# Revit family: МФУ, копир настольный формата А3
name_source: partatom
category: Оборудование
revit_build: Autodesk Revit 2017 (Build: 20170419_0315(x64)
units: mm (PartAtom-declared; Revit-internal decimal feet)

## family parameters
Всегда вертикально = Да
На основе рабочей плоскости = Нет
Общий = Нет
При загрузке вырезать с полостями = Нет
Размер круглого соединителя = Использовать диаметр
Тип детали = Нормальный
Точка расчета площади = Нет

## types (1)
- -
    bialy = xero_szary
    blekitny = xero_blekitny
    czerwony = xero_czerwony
    lcd = xero_lcd
    niebieski ciemniejszy majtkowy = xero_ciemniejsze majty
    niebieski ciemny przycisk = xero_niebieski przycisk
    niebieski majtkowy = xero_niebieski majtkowy
    niebieskie szkolo = Glass, Green
    Высота = 558 мм
    Глубина = 587 мм
    Единицы = шт.
    Задание = ЭМ
    Изготовитель = Severin
    Мощность номинальная = 1000 Вт
    Наименование = Многофункциональное устройство формата А3
    Напряжение = 220 В
    Число полюсов = 1
    Ширина = 568 мм

## geometry (parser evidence)
native form markers: Sweep x3
no freeform markers — native parametric forms only
